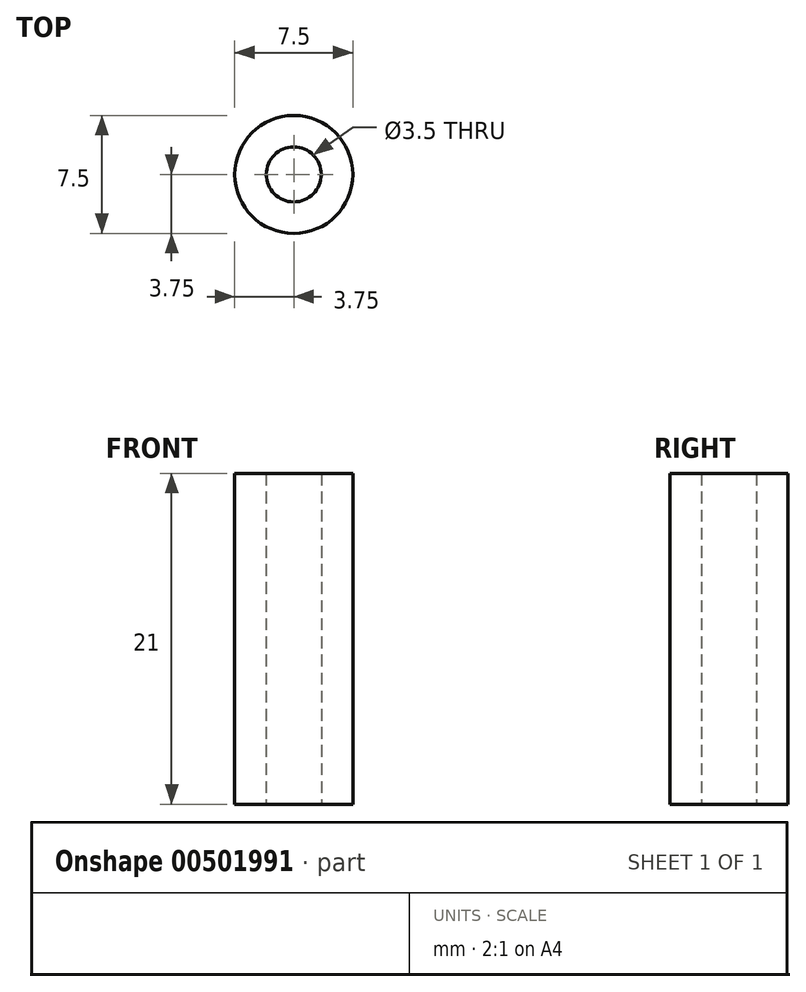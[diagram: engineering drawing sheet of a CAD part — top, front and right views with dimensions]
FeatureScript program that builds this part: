
annotation { "Feature Type Name" : "Feature", "Feature Type Description" : "" }
export const myFeature = defineFeature(function(context is Context, id is Id, definition is map)
    precondition{}
    {
        {
            var Q0;
            Q0=qCreatedBy(makeId("Top.planeOp"),FACE);
            var sketch = newSketch(context, id + "F0", { "sketchPlane" : qUnion([Q0])});
            skCircle(sketch, "E0", {"center": v(0, 0) * mm, "radius": 3.75 * mm});
            skCircle(sketch, "E1", {"center": v(0, 0) * mm, "radius": 1.75 * mm});
            skSolve(sketch);
        }
        {
            var Q0;
            Q0=makeQuery(id+"F0.imprint","IMPRINT",FACE,{"disambiguationData":[TD([[makeQuery(id+"F0.imprint","IMPRINT",EDGE,{"derivedFrom":sQuery(id+"F0.wireOp",EDGE,"E0")}),1.0]])]});
            extrude(context, id + "F1", {"entities" : qUnion([Q0]), "depth" : 21 * mm});
        }
    });
